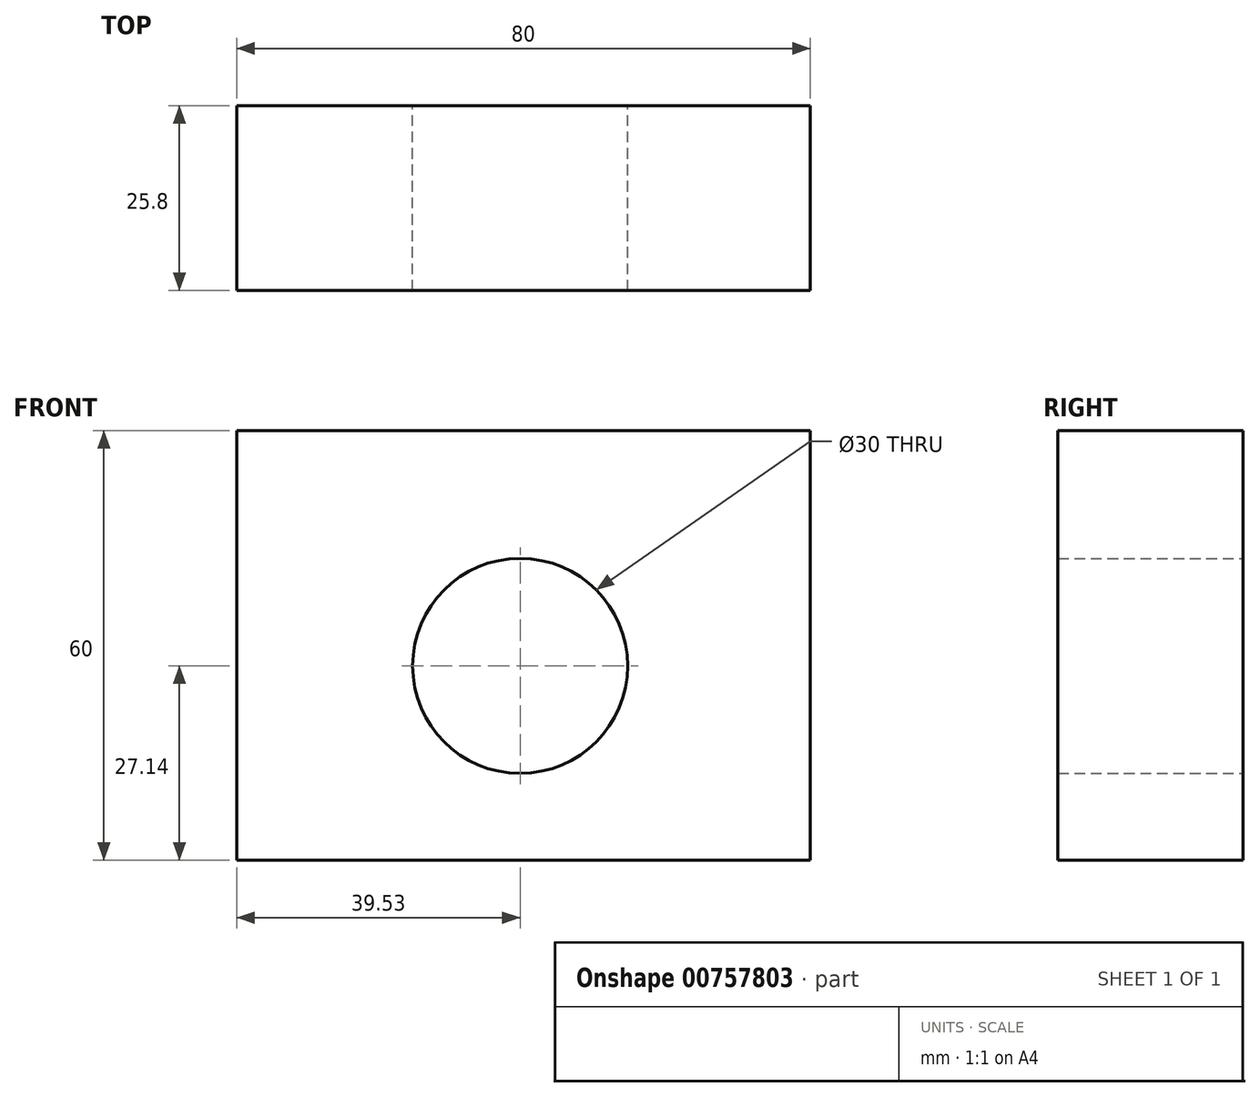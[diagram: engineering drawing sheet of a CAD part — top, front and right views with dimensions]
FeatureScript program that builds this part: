
annotation { "Feature Type Name" : "Feature", "Feature Type Description" : "" }
export const myFeature = defineFeature(function(context is Context, id is Id, definition is map)
    precondition{}
    {
        {
            var Q0;
            Q0=qCreatedBy(makeId("Front.planeOp"),FACE);
            var sketch = newSketch(context, id + "F0", { "sketchPlane" : qUnion([Q0])});
            skCircle(sketch, "E0", {"center": v(0, 0) * mm, "radius": 15 * mm});
            skLineSegment(sketch, "E1.bottom", {"start": v(-39.53, 32.86) * mm, "end": v(40.47, 32.86) * mm});
            skLineSegment(sketch, "E1.top", {"start": v(-39.53, -27.14) * mm, "end": v(40.47, -27.14) * mm});
            skLineSegment(sketch, "E1.left", {"start": v(-39.53, 32.86) * mm, "end": v(-39.53, -27.14) * mm});
            skLineSegment(sketch, "E1.right", {"start": v(40.47, 32.86) * mm, "end": v(40.47, -27.14) * mm});
            skSolve(sketch);
        }
        {
            var Q0;
            Q0 = qSketchRegion(id + "F0", true);
            extrude(context, id + "F1", {"entities" : qUnion([Q0]), "depth" : 25.8 * mm, "offsetDistance" : 25 * mm});
        }
    });
